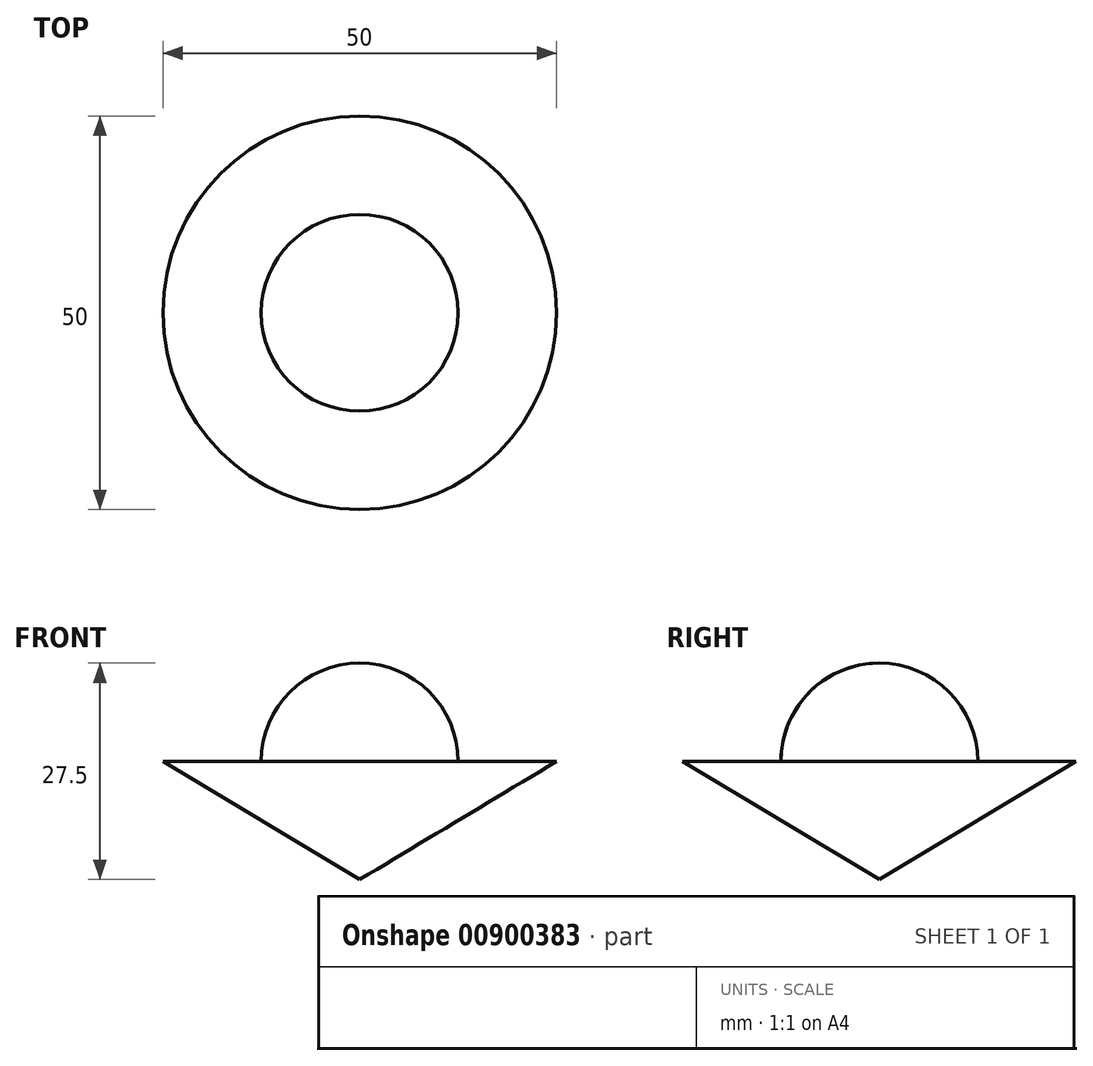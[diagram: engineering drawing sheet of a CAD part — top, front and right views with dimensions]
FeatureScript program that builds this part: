
annotation { "Feature Type Name" : "Feature", "Feature Type Description" : "" }
export const myFeature = defineFeature(function(context is Context, id is Id, definition is map)
    precondition{}
    {
        {
            var Q0;
            Q0=qCreatedBy(makeId("Right.planeOp"),FACE);
            var sketch = newSketch(context, id + "F0", { "sketchPlane" : qUnion([Q0])});
            skLineSegment(sketch, "E0", {"start": v(0, 0) * mm, "end": v(0, 15) * mm});
            skLineSegment(sketch, "E1", {"start": v(0, 15) * mm, "end": v(25, 15) * mm});
            skLineSegment(sketch, "E2", {"start": v(25, 15) * mm, "end": v(0, 0) * mm});
            skSolve(sketch);
        }
        {
            var Q0;
            Q0=makeQuery(id+"F0.imprint","IMPRINT",FACE,{"disambiguationData":[TD([[makeQuery(id+"F0.imprint","IMPRINT",EDGE,{"derivedFrom":sQuery(id+"F0.wireOp",EDGE,"E0")}),-1.0]])]});
            var Q1;
            Q1=sQuery(id+"F0.wireOp",EDGE,"E0");
            revolve(context, id + "F1", {"surfaceOperationType" : NewSurfaceOperationType.NEW, "entities" : qUnion([Q0]), "axis" : qUnion([Q1]), "revolveType" : RevolveType.FULL});
        }
        {
            var Q0;
            Q0=qCreatedBy(makeId("Right.planeOp"),FACE);
            var sketch = newSketch(context, id + "F2", { "sketchPlane" : qUnion([Q0])});
            skLineSegment(sketch, "E3", {"start": v(0, 0) * mm, "end": v(0, 49.5) * mm});
            skCircle(sketch, "E4", {"center": v(0, 15) * mm, "radius": 12.5 * mm});
            skPoint(sketch, "E5", {"position": v(0, 24.75) * mm});
            skSolve(sketch);
        }
        {
            var Q0;
            {var subQ0=sQuery(id+"F2.wireOp",EDGE,"E4");var subQ1=sQuery(id+"F2.wireOp",EDGE,"E3");var subQ2=makeQuery(id+"F2.imprint","INTERSECT",VERTEX,{"disambiguationData":[OD(0.0)],"derivedFrom":[subQ1,subQ0]});Q0=makeQuery(id+"F2.imprint","IMPRINT",FACE,{"disambiguationData":[TD([[makeQuery(id+"F2.imprint","IMPRINT",EDGE,{"disambiguationData":[TD([[subQ2,-1.0]])],"derivedFrom":subQ1}),-1.0]])]});}
            var Q1;
            Q1=sQuery(id+"F2.wireOp",EDGE,"E3");
            revolve(context, id + "F3", {"operationType" : NewBodyOperationType.ADD, "surfaceOperationType" : NewSurfaceOperationType.NEW, "entities" : qUnion([Q0]), "axis" : qUnion([Q1]), "revolveType" : RevolveType.FULL});
        }
    });
